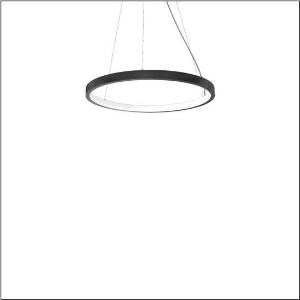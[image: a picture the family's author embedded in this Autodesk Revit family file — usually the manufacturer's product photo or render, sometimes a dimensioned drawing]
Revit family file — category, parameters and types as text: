
# Revit family: silica_r__21_ring-i_5pjbi2d1104a_14c4
name_source: partatom
category: Lighting Fixtures
units: mm (PartAtom-declared; Revit-internal decimal feet)

## family parameters
Cut with Voids When Loaded = No
Host = Face
Light Source = No
Part Type = Normal
Room Calculation Point = No
Round Connector Dimension = Use Diameter
Shared = No

## types (1)
- Silica® 21 Ring-I (1 x LED, 4800 lm, 80 W, 3000K)
    Apparent Load = 80 VA
    CIE Flux Codes = 22 48 76 50 101
    Color Rendering = 80
    Color Temperature = 3000K
    Default Elevation = 1800 mm
    Description = Silica® 21 Ring-I, suspended luminaire, of PMMA, frosted, light emission: inner ring side luminous distribution, primary light characteristic: symmetric, installation type: suspended mounting, LED, rated luminous flux: 4.800lm, luminous efficacy: 60lm/W, light colour: 830, colour temperature: 3000K, with terminal, 5-pole, mains connection: 230V, AC/DC, 0/50..60Hz, rated input power: 80W, housing, of extruded aluminium section, jet black (RAL 9005), diameter: 805mm, ceiling canopy, jet black (RAL 9005), protection rating (lamp compartment): IP40, insulation class (complete): insulation class I (protective earthing), certification: CE, impact resistance: IK02, permissible operating ambient temperature: 0..+35°C, packaging unit: 1 piece
    Height = 48 mm  [stored 0.15748 ft]
    Lamp = 1 x LED
    Lamp Light Flux = 4800 lm
    Lamp Power = 80 W
    Lamp count = 1
    Length = 805 mm
    Luminous efficacy = 60 lm/W
    Manufacturer = Siteco
    ModVariant = No
    Model = 5PJBI2D1104A
    Mounting Place = Ceiling
    Mounting Type = Pendant
    Number of Poles = 1
    OnlyDefault = Yes
    Power Factor = 1
    Product Name = Silica® 21 Ring-I
    Product group = suspended luminaire
    ProductGroupID = 904
    Protection Class = Protection class I
    Protection Degree = IP 40
    RLX_Detail_Level = 1
    RLX_Emergency_Light_Flux = 0 lm
    RLX_Emergency_Type = 0
    RLX_Emergency_Type_DB = No
    RlxData = <blob elided: 13913 chars, md5=20a81e45>
    Socket = socket
    Standby Power = 0 W
    System Light Flux = 4800 lm
    System Power = 80 W
    Type Comments = Product without accessories
    Type Image = l_1258365.jpg
    URL = http://relux.com
    VarID = ---
    Voltage = 0 V
    Weight = 0.00 kg
    Width = 0 mm  [stored 0 ft]

note: [stored X ft] marks values corroborated as IEEE doubles in the binary element streams (Revit-internal decimal feet)

## geometry (parser evidence)
native form markers: Sweep x15
no freeform markers — native parametric forms only
